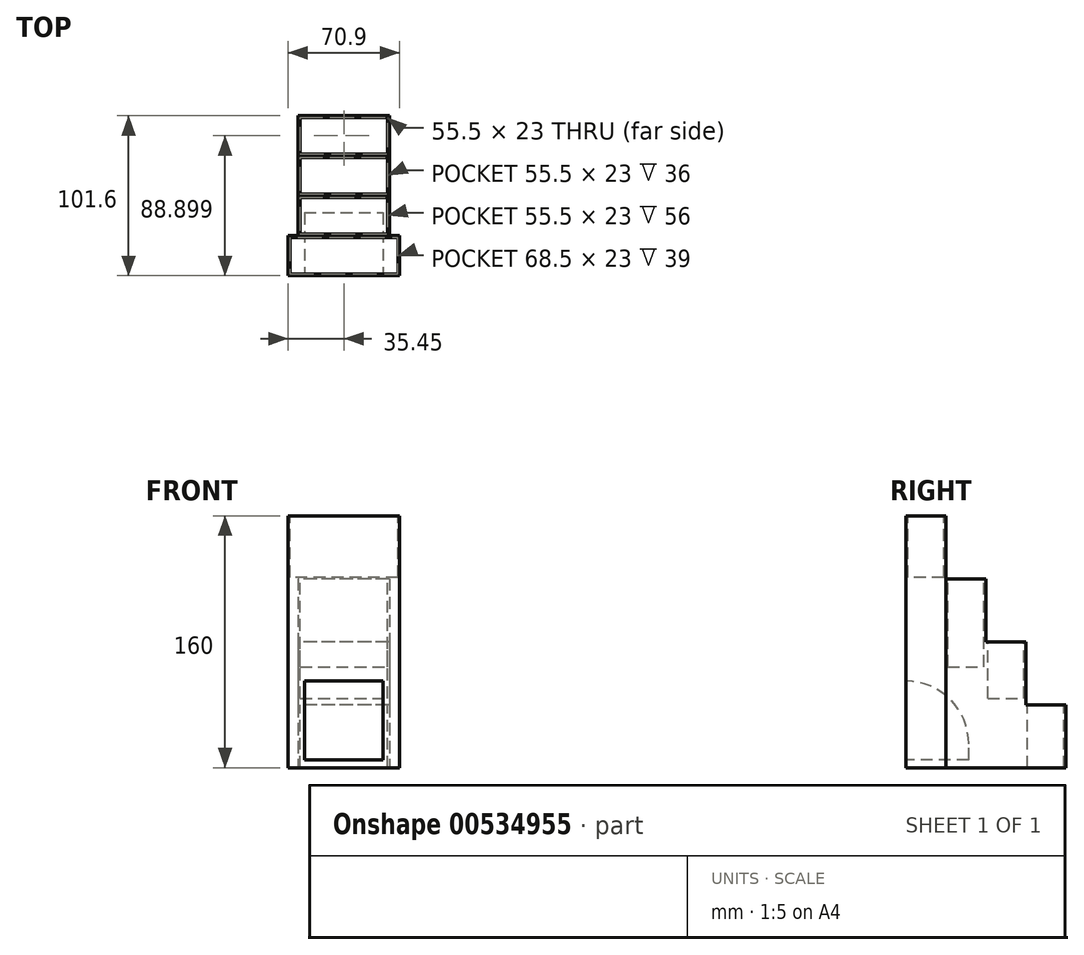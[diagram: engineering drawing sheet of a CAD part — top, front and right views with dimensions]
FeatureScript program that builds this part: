
annotation { "Feature Type Name" : "Feature", "Feature Type Description" : "" }
export const myFeature = defineFeature(function(context is Context, id is Id, definition is map)
    precondition{}
    {
        {
            var Q0;
            Q0=qCreatedBy(makeId("Right.planeOp"),FACE);
            var sketch = newSketch(context, id + "F0", { "sketchPlane" : qUnion([Q0])});
            skLineSegment(sketch, "E0", {"start": v(-150.2, 0) * mm, "end": v(-150.2, 160) * mm});
            skLineSegment(sketch, "E1", {"start": v(-150.2, 160) * mm, "end": v(-124.8, 160) * mm});
            skLineSegment(sketch, "E2", {"start": v(-124.8, 160) * mm, "end": v(-124.8, 120) * mm});
            skLineSegment(sketch, "E3", {"start": v(-124.8, 120) * mm, "end": v(-99.4, 120) * mm});
            skLineSegment(sketch, "E4", {"start": v(-99.4, 120) * mm, "end": v(-99.4, 80) * mm});
            skLineSegment(sketch, "E5", {"start": v(-99.4, 80) * mm, "end": v(-74, 80) * mm});
            skLineSegment(sketch, "E6", {"start": v(-74, 80) * mm, "end": v(-74, 40) * mm});
            skLineSegment(sketch, "E7", {"start": v(-74, 40) * mm, "end": v(-48.6, 40) * mm});
            skLineSegment(sketch, "E8", {"start": v(-48.6, 40) * mm, "end": v(-48.6, 0) * mm});
            skLineSegment(sketch, "E9", {"start": v(-48.6, 0) * mm, "end": v(-150.2, 0) * mm});
            skLineSegment(sketch, "E10", {"start": v(-124.8, 120) * mm, "end": v(-124.8, 0) * mm});
            skSolve(sketch);
        }
        {
            var Q0;
            Q0=makeQuery(id+"F0.imprint","IMPRINT",FACE,{"disambiguationData":[TD([[makeQuery(id+"F0.imprint","IMPRINT",EDGE,{"derivedFrom":sQuery(id+"F0.wireOp",EDGE,"E3")}),-1.0]])]});
            extrude(context, id + "F1", {"entities" : qUnion([Q0]), "depth" : 57.9 * mm, "offsetDistance" : 25 * mm});
        }
        {
            var Q0;
            {var subQ1=sQuery(id+"F0.wireOp",EDGE,"E0");Q0=makeQuery(id+"F0.imprint","IMPRINT",FACE,{"disambiguationData":[TD([[makeQuery(id+"F0.imprint","IMPRINT",EDGE,{"derivedFrom":subQ1}),-1.0]])]});}
            extrude(context, id + "F2", {"entities" : qUnion([Q0]), "operationType" : NewBodyOperationType.ADD, "depth" : 64.4 * mm, "offsetDistance" : 25 * mm, "hasSecondDirection" : true, "secondDirectionOppositeDirection" : true, "secondDirectionDepth" : 6.5 * mm});
        }
        {
            var Q0;
            Q0=makeQuery(id+"F2.opExtrude","SWEPT_FACE",FACE,{"disambiguationData":[OSD([sQuery(id+"F0.wireOp",EDGE,"E1")])]});
            var sketch = newSketch(context, id + "F3", { "sketchPlane" : qUnion([Q0])});
            skLineSegment(sketch, "E11.0", {"start": v(-5.3, -126) * mm, "end": v(-5.3, -149) * mm});
            skLineSegment(sketch, "E11.1", {"start": v(63.2, -126) * mm, "end": v(-5.3, -126) * mm});
            skLineSegment(sketch, "E11.2", {"start": v(63.2, -149) * mm, "end": v(63.2, -126) * mm});
            skLineSegment(sketch, "E11.3", {"start": v(-5.3, -149) * mm, "end": v(63.2, -149) * mm});
            skLineSegment(sketch, "E12.0", {"start": v(1.2, -100.6) * mm, "end": v(1.2, -123.6) * mm});
            skLineSegment(sketch, "E12.1", {"start": v(56.7, -100.6) * mm, "end": v(1.2, -100.6) * mm});
            skLineSegment(sketch, "E12.2", {"start": v(56.7, -123.6) * mm, "end": v(56.7, -100.6) * mm});
            skLineSegment(sketch, "E12.3", {"start": v(1.2, -123.6) * mm, "end": v(56.7, -123.6) * mm});
            skLineSegment(sketch, "E13.0", {"start": v(1.2, -75.2) * mm, "end": v(1.2, -98.2) * mm});
            skLineSegment(sketch, "E13.1", {"start": v(56.7, -75.2) * mm, "end": v(1.2, -75.2) * mm});
            skLineSegment(sketch, "E13.2", {"start": v(56.7, -98.2) * mm, "end": v(56.7, -75.2) * mm});
            skLineSegment(sketch, "E13.3", {"start": v(1.2, -98.2) * mm, "end": v(56.7, -98.2) * mm});
            skLineSegment(sketch, "E14.0", {"start": v(1.2, -49.8) * mm, "end": v(1.2, -72.8) * mm});
            skLineSegment(sketch, "E14.1", {"start": v(56.7, -49.8) * mm, "end": v(1.2, -49.8) * mm});
            skLineSegment(sketch, "E14.2", {"start": v(56.7, -72.8) * mm, "end": v(56.7, -49.8) * mm});
            skLineSegment(sketch, "E14.3", {"start": v(1.2, -72.8) * mm, "end": v(56.7, -72.8) * mm});
            skSolve(sketch);
        }
        {
            var Q0;
            Q0=makeQuery(id+"F3.imprint","IMPRINT",FACE,{"disambiguationData":[TD([[makeQuery(id+"F3.imprint","IMPRINT",EDGE,{"derivedFrom":sQuery(id+"F3.wireOp",EDGE,"E14.0")}),1.0]])]});
            extrude(context, id + "F4", {"entities" : qUnion([Q0]), "operationType" : NewBodyOperationType.REMOVE, "oppositeDirection" : true, "depth" : 207 * mm, "offsetDistance" : 25 * mm});
        }
        {
            var Q0;
            Q0=makeQuery(id+"F3.imprint","IMPRINT",FACE,{"disambiguationData":[TD([[makeQuery(id+"F3.imprint","IMPRINT",EDGE,{"derivedFrom":sQuery(id+"F3.wireOp",EDGE,"E13.0")}),1.0]])]});
            var Q1;
            Q1=makeQuery(id+"F1.opExtrude","SWEPT_FACE",FACE,{"disambiguationData":[OSD([sQuery(id+"F0.wireOp",EDGE,"E5")])]});
            extrude(context, id + "F5", {"entities" : qUnion([Q0]), "operationType" : NewBodyOperationType.REMOVE, "endBound" : BoundingType.UP_TO_SURFACE, "oppositeDirection" : true, "depth" : 25 * mm, "endBoundEntityFace" : qUnion([Q1]), "hasOffset" : true, "offsetDistance" : -36 * mm});
        }
        {
            var Q0;
            Q0=makeQuery(id+"F3.imprint","IMPRINT",FACE,{"disambiguationData":[TD([[makeQuery(id+"F3.imprint","IMPRINT",EDGE,{"derivedFrom":sQuery(id+"F3.wireOp",EDGE,"E12.0")}),1.0]])]});
            var Q1;
            Q1=makeQuery(id+"F1.opExtrude","SWEPT_FACE",FACE,{"disambiguationData":[OSD([sQuery(id+"F0.wireOp",EDGE,"E3")])]});
            extrude(context, id + "F6", {"entities" : qUnion([Q0]), "operationType" : NewBodyOperationType.REMOVE, "endBound" : BoundingType.UP_TO_SURFACE, "oppositeDirection" : true, "depth" : 25 * mm, "endBoundEntityFace" : qUnion([Q1]), "hasOffset" : true, "offsetDistance" : -56 * mm});
        }
        {
            var Q0;
            Q0=makeQuery(id+"F3.imprint","IMPRINT",FACE,{"disambiguationData":[TD([[makeQuery(id+"F3.imprint","IMPRINT",EDGE,{"derivedFrom":sQuery(id+"F3.wireOp",EDGE,"E11.0")}),1.0]])]});
            extrude(context, id + "F7", {"entities" : qUnion([Q0]), "operationType" : NewBodyOperationType.REMOVE, "depth" : -39 * mm, "offsetDistance" : 25 * mm});
        }
        {
            var Q0;
            Q0=makeQuery(id+"F2.opExtrude","SWEPT_FACE",FACE,{"disambiguationData":[OSD([sQuery(id+"F0.wireOp",EDGE,"E0")])]});
            var sketch = newSketch(context, id + "F8", { "sketchPlane" : qUnion([Q0])});
            skLineSegment(sketch, "E15.bottom", {"start": v(3.95, 5) * mm, "end": v(53.95, 5) * mm});
            skLineSegment(sketch, "E15.top", {"start": v(3.95, 55) * mm, "end": v(53.95, 55) * mm});
            skLineSegment(sketch, "E15.left", {"start": v(3.95, 5) * mm, "end": v(3.95, 55) * mm});
            skLineSegment(sketch, "E15.right", {"start": v(53.95, 5) * mm, "end": v(53.95, 55) * mm});
            skSolve(sketch);
        }
        {
            var Q0;
            Q0=makeQuery(id+"F8.imprint","IMPRINT",FACE,{"disambiguationData":[TD([[makeQuery(id+"F8.imprint","IMPRINT",EDGE,{"derivedFrom":sQuery(id+"F8.wireOp",EDGE,"E15.bottom")}),1.0]])]});
            extrude(context, id + "F9", {"entities" : qUnion([Q0]), "operationType" : NewBodyOperationType.REMOVE, "oppositeDirection" : true, "depth" : 40 * mm, "offsetDistance" : 25 * mm});
        }
        {
            var Q0;
            Q0=makeQuery(id+"F9.boolean.opBoolean","COPY",EDGE,{"derivedFrom":makeQuery(id+"F9.opExtrude","CAP_EDGE",EDGE,{"disambiguationData":[OSD([sQuery(id+"F8.wireOp",EDGE,"E15.top")])],"isStart":false})});
            fillet(context, id + "F10", {"entities" : qUnion([Q0]), "radius" : 40 * mm, "tangentPropagation" : true, "allowEdgeOverflow" : false});
        }
    });
